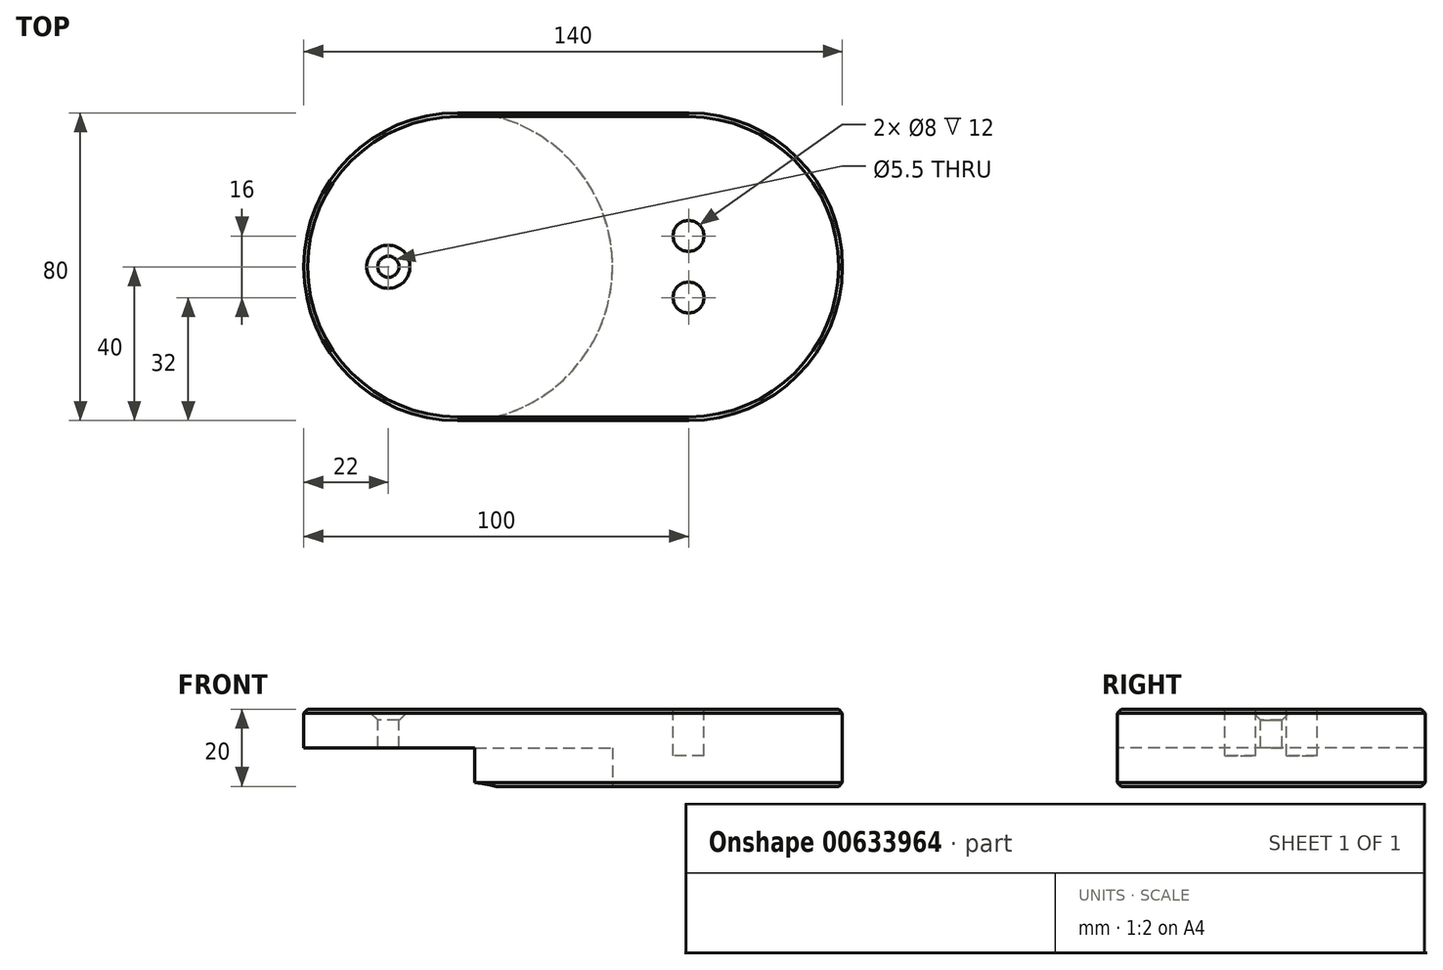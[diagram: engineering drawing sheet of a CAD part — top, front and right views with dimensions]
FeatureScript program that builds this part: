
annotation { "Feature Type Name" : "Feature", "Feature Type Description" : "" }
export const myFeature = defineFeature(function(context is Context, id is Id, definition is map)
    precondition{}
    {
        {
            var Q0;
            Q0=qCreatedBy(makeId("Top.planeOp"),FACE);
            var sketch = newSketch(context, id + "F0", { "sketchPlane" : qUnion([Q0])});
            skArc(sketch, "E0", {"start": v(0, 40) * mm, "mid": v(-40, 0) * mm, "end": v(0, -40) * mm});
            skLineSegment(sketch, "E1", {"start": v(0, 0) * mm, "end": v(0, 40) * mm, "construction": true});
            skLineSegment(sketch, "E2", {"start": v(0, 0) * mm, "end": v(60, 0) * mm, "construction": true});
            skLineSegment(sketch, "E3", {"start": v(0, -40) * mm, "end": v(0, 0) * mm, "construction": true});
            skArc(sketch, "E4", {"start": v(60, -40) * mm, "mid": v(100, 0) * mm, "end": v(60, 40) * mm});
            skLineSegment(sketch, "E5", {"start": v(0, 40) * mm, "end": v(60, 40) * mm});
            skLineSegment(sketch, "E6", {"start": v(0, -40) * mm, "end": v(60, -40) * mm});
            skLineSegment(sketch, "E7", {"start": v(60, 0) * mm, "end": v(60, 40) * mm, "construction": true});
            skLineSegment(sketch, "E8", {"start": v(60, 0) * mm, "end": v(60, -40) * mm, "construction": true});
            skSolve(sketch);
        }
        {
            var Q0;
            {var subQ1=sQuery(id+"F0.wireOp",EDGE,"V8RzuikD-NFWa-RmP1-21VH-X3Mqi6nUnLhn.bottom");Q0=makeQuery(id+"F0.imprint","IMPRINT",FACE,{"disambiguationData":[TD([[makeQuery(id+"F0.imprint","IMPRINT",EDGE,{"derivedFrom":subQ1}),-1.0]])]});}
            var Q1;
            Q1=makeQuery(id+"F0.imprint","IMPRINT",FACE,{"disambiguationData":[TD([[makeQuery(id+"F0.imprint","IMPRINT",EDGE,{"derivedFrom":sQuery(id+"F0.wireOp",EDGE,"E0")}),1.0]])]});
            extrude(context, id + "F1", {"entities" : qUnion([Q0, Q1]), "oppositeDirection" : true, "depth" : 20 * mm, "offsetDistance" : 25 * mm});
        }
        {
            var Q0;
            Q0=makeQuery(id+"F1.opExtrude","CAP_FACE",FACE,{"disambiguationData":[OSD([sQuery(id+"F0.wireOp",EDGE,"E0"),sQuery(id+"F0.wireOp",EDGE,"E4"),sQuery(id+"F0.wireOp",EDGE,"E5"),sQuery(id+"F0.wireOp",EDGE,"E6")])],"isStart":false});
            var sketch = newSketch(context, id + "F2", { "sketchPlane" : qUnion([Q0])});
            skCircle(sketch, "E9", {"center": v(0, 0) * mm, "radius": 40.25 * mm});
            skSolve(sketch);
        }
        {
            var Q0;
            {var subQ2=sQuery(id+"F0.wireOp",EDGE,"E0");var subQ5=makeQuery(id+"F1.opExtrude","CAP_EDGE",EDGE,{"disambiguationData":[OSD([subQ2])],"isStart":false});Q0=makeQuery(id+"F2.imprint","IMPRINT",FACE,{"disambiguationData":[TD([[makeQuery(id+"F2.imprint","IMPRINT",EDGE,{"derivedFrom":subQ5}),-1.0]])]});}
            extrude(context, id + "F3", {"entities" : qUnion([Q0]), "operationType" : NewBodyOperationType.REMOVE, "oppositeDirection" : true, "depth" : 10 * mm, "offsetDistance" : 25 * mm});
        }
        {
            var Q0;
            Q0=makeQuery(id+"F1.opExtrude","CAP_FACE",FACE,{"disambiguationData":[OSD([sQuery(id+"F0.wireOp",EDGE,"E0"),sQuery(id+"F0.wireOp",EDGE,"nQ46CTho-IiNY-G00n-m9E3-fDT1SJuTAcHe"),sQuery(id+"F0.wireOp",EDGE,"RIUWROrT-wQFf-Y0j8-5Ued-bYEgcayq2syn"),sQuery(id+"F0.wireOp",EDGE,"PchVJb6p-P77d-iEiP-Ag3m-YXKHloptU5RG")])],"isStart":true});
            var sketch = newSketch(context, id + "F4", { "sketchPlane" : qUnion([Q0])});
            skLineSegment(sketch, "E10", {"start": v(0, 0) * mm, "end": v(-18, 0) * mm, "construction": true});
            skSolve(sketch);
        }
        {
            var Q0;
            Q0=sQuery(id+"F4.wireOp",VERTEX,"E10.end");
            var Q1;
            Q1=makeQuery(id+"F1.opExtrude","SWEPT_BODY",BODY,{"disambiguationData":[OSD([sQuery(id+"F0.wireOp",EDGE,"E0"),sQuery(id+"F0.wireOp",EDGE,"nQ46CTho-IiNY-G00n-m9E3-fDT1SJuTAcHe"),sQuery(id+"F0.wireOp",EDGE,"RIUWROrT-wQFf-Y0j8-5Ued-bYEgcayq2syn"),sQuery(id+"F0.wireOp",EDGE,"PchVJb6p-P77d-iEiP-Ag3m-YXKHloptU5RG")])]});
            hole(context, id + "F5", {"style" : HoleStyle.C_SINK, "endStyle" : HoleEndStyle.THROUGH, "standardTappedOrClearance" : lookupTablePath({ "standard" : "ISO", "fit" : "Normal", "size" : "M5", "type" : "Clearance" }), "standardBlindInLast" : lookupTablePath({ "fit" : "Standard", "standard" : "ISO", "size" : "M5", "type" : "Clearance" }), "holeDiameter" : 5.5 * mm, "cSinkDiameter" : 11.2 * mm, "cSinkAngle" : 90 * degree, "majorDiameter" : 5 * mm, "isTappedThrough" : true, "tappedDepth" : 12 * mm, "tapClearance" : 3, "locations" : qUnion([Q0]), "scope" : qUnion([Q1])});
        }
        {
            var Q0;
            Q0=qCreatedBy(makeId("Front.planeOp"),FACE);
            var sketch = newSketch(context, id + "F6", { "sketchPlane" : qUnion([Q0])});
            skLineSegment(sketch, "E11", {"start": v(0, 0) * mm, "end": v(0, 32.46) * mm, "construction": true});
            skSolve(sketch);
        }
        {
            var Q0;
            Q0=makeQuery(id+"F1.opExtrude","CAP_FACE",FACE,{"disambiguationData":[OSD([sQuery(id+"F0.wireOp",EDGE,"E0"),sQuery(id+"F0.wireOp",EDGE,"E4"),sQuery(id+"F0.wireOp",EDGE,"E5"),sQuery(id+"F0.wireOp",EDGE,"E6")])],"isStart":true});
            var sketch = newSketch(context, id + "F7", { "sketchPlane" : qUnion([Q0])});
            skLineSegment(sketch, "E12", {"start": v(60, 8) * mm, "end": v(60, -8) * mm, "construction": true});
            skPoint(sketch, "E13", {"position": v(60, 0) * mm});
            skCircle(sketch, "E14", {"center": v(60, -8) * mm, "radius": 4 * mm});
            skCircle(sketch, "E15", {"center": v(60, 8) * mm, "radius": 4 * mm});
            skSolve(sketch);
        }
        {
            var Q0;
            Q0=makeQuery(id+"F7.imprint","IMPRINT",FACE,{"disambiguationData":[TD([[makeQuery(id+"F7.imprint","IMPRINT",EDGE,{"derivedFrom":sQuery(id+"F7.wireOp",EDGE,"E15")}),1.0]])]});
            var Q1;
            Q1=makeQuery(id+"F7.imprint","IMPRINT",FACE,{"disambiguationData":[TD([[makeQuery(id+"F7.imprint","IMPRINT",EDGE,{"derivedFrom":sQuery(id+"F7.wireOp",EDGE,"E14")}),1.0]])]});
            extrude(context, id + "F8", {"entities" : qUnion([Q0, Q1]), "operationType" : NewBodyOperationType.REMOVE, "oppositeDirection" : true, "depth" : 12 * mm, "offsetDistance" : 25 * mm});
        }
        {
            var Q0;
            Q0=makeQuery(id+"F3.boolean.opBoolean","COPY",EDGE,{"derivedFrom":makeQuery(id+"F3.opExtrude","CAP_EDGE",EDGE,{"disambiguationData":[OSD([sQuery(id+"F2.wireOp",EDGE,"E9")])],"isStart":true})});
            var Q1;
            Q1=makeQuery(id+"F1.opExtrude","CAP_EDGE",EDGE,{"disambiguationData":[OSD([sQuery(id+"F0.wireOp",EDGE,"E4")])],"isStart":false});
            var Q2;
            Q2=makeQuery(id+"F3.boolean.opBoolean","COPY",EDGE,{"derivedFrom":makeQuery(id+"F3.opExtrude","SWEPT_EDGE",EDGE,{"disambiguationData":[OSD([sQuery(id+"F0.wireOp",EDGE,"E5"),sQuery(id+"F2.wireOp",EDGE,"E9")])]})});
            var Q3;
            Q3=makeQuery(id+"F3.boolean.opBoolean","COPY",EDGE,{"derivedFrom":makeQuery(id+"F3.opExtrude","SWEPT_EDGE",EDGE,{"disambiguationData":[OSD([sQuery(id+"F0.wireOp",EDGE,"E6"),sQuery(id+"F2.wireOp",EDGE,"E9")])]})});
            var Q4;
            Q4=makeQuery(id+"F3.boolean.opBoolean","COPY",EDGE,{"derivedFrom":makeQuery(id+"F3.opExtrude","CAP_EDGE",EDGE,{"disambiguationData":[OSD([sQuery(id+"F0.wireOp",EDGE,"E0")])],"isStart":false})});
            var Q5;
            Q5=makeQuery(id+"F1.opExtrude","CAP_EDGE",EDGE,{"disambiguationData":[OSD([sQuery(id+"F0.wireOp",EDGE,"E5")])],"isStart":true});
            var Q6;
            Q6=makeQuery(id+"F8.boolean.opBoolean","COPY",EDGE,{"derivedFrom":makeQuery(id+"F8.opExtrude","CAP_EDGE",EDGE,{"disambiguationData":[OSD([sQuery(id+"F7.wireOp",EDGE,"KDhvstXq-sJ7e-TKGl-rVB3-imwFkszLSQl6")])],"isStart":true})});
            var Q7;
            Q7=makeQuery(id+"F8.boolean.opBoolean","COPY",EDGE,{"derivedFrom":makeQuery(id+"F8.opExtrude","CAP_EDGE",EDGE,{"disambiguationData":[OSD([sQuery(id+"F7.wireOp",EDGE,"E14")])],"isStart":true})});
            var Q8;
            Q8=makeQuery(id+"F8.boolean.opBoolean","COPY",EDGE,{"derivedFrom":makeQuery(id+"F8.opExtrude","CAP_EDGE",EDGE,{"disambiguationData":[OSD([sQuery(id+"F7.wireOp",EDGE,"E15")])],"isStart":true})});
            chamfer(context, id + "F9", {"entities" : qUnion([Q0, Q1, Q2, Q3, Q4, Q5, Q6, Q7, Q8]), "width" : 1 * mm, "tangentPropagation" : true});
        }
    });
